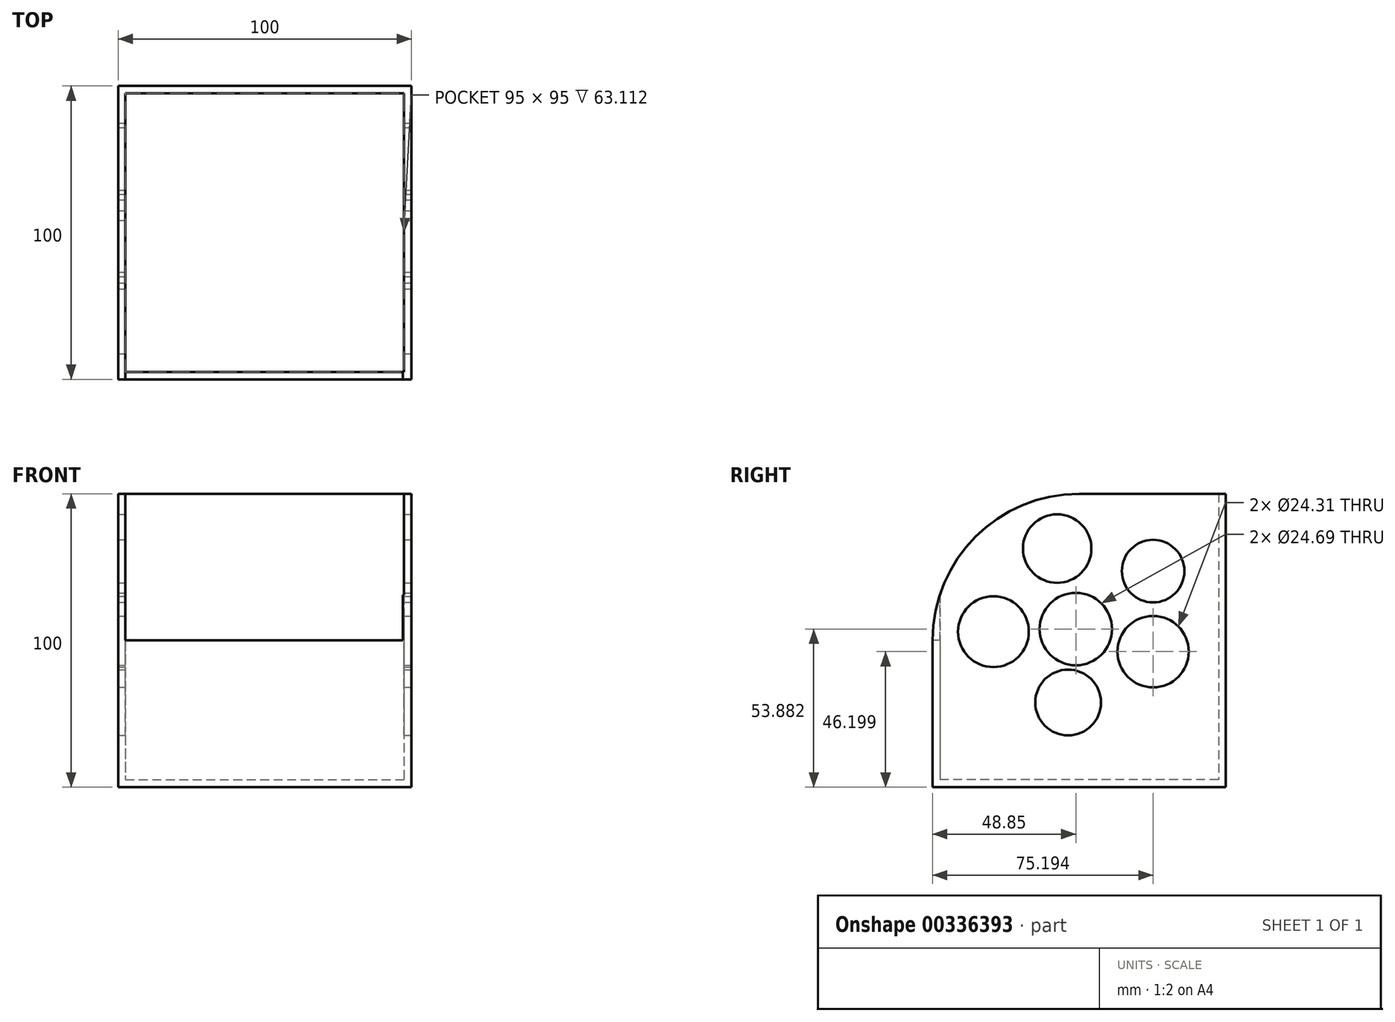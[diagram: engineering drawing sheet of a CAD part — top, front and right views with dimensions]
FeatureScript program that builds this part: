
annotation { "Feature Type Name" : "Feature", "Feature Type Description" : "" }
export const myFeature = defineFeature(function(context is Context, id is Id, definition is map)
    precondition{}
    {
        {
            var Q0;
            Q0=qCreatedBy(makeId("Top.planeOp"),FACE);
            var sketch = newSketch(context, id + "F0", { "sketchPlane" : qUnion([Q0])});
            skLineSegment(sketch, "E0.bottom", {"start": v(-69.43, 51.15) * mm, "end": v(30.57, 51.15) * mm});
            skLineSegment(sketch, "E0.top", {"start": v(-69.43, -48.85) * mm, "end": v(30.57, -48.85) * mm});
            skLineSegment(sketch, "E0.left", {"start": v(-69.43, 51.15) * mm, "end": v(-69.43, -48.85) * mm});
            skLineSegment(sketch, "E0.right", {"start": v(30.57, 51.15) * mm, "end": v(30.57, -48.85) * mm});
            skSolve(sketch);
        }
        {
            var Q0;
            Q0=makeQuery(id+"F0.imprint","IMPRINT",FACE,{"disambiguationData":[TD([[makeQuery(id+"F0.imprint","IMPRINT",EDGE,{"derivedFrom":sQuery(id+"F0.wireOp",EDGE,"E0.bottom")}),-1.0]])]});
            extrude(context, id + "F1", {"entities" : qUnion([Q0]), "depth" : 100 * mm});
        }
        {
            var Q0;
            Q0=makeQuery(id+"F1.opExtrude","CAP_FACE",FACE,{"disambiguationData":[OSD([sQuery(id+"F0.wireOp",EDGE,"E0.bottom"),sQuery(id+"F0.wireOp",EDGE,"E0.top"),sQuery(id+"F0.wireOp",EDGE,"E0.left"),sQuery(id+"F0.wireOp",EDGE,"E0.right")])],"isStart":false});
            shell(context, id + "F2", {"entities" : qUnion([Q0]), "thickness" : 2.5 * mm});
        }
        {
            var Q0;
            Q0=makeQuery(id+"F1.opExtrude","CAP_FACE",FACE,{"disambiguationData":[OSD([sQuery(id+"F0.wireOp",EDGE,"E0.bottom"),sQuery(id+"F0.wireOp",EDGE,"E0.top"),sQuery(id+"F0.wireOp",EDGE,"E0.left"),sQuery(id+"F0.wireOp",EDGE,"E0.right")])],"isStart":false});
            var sketch = newSketch(context, id + "F3", { "sketchPlane" : qUnion([Q0])});
            skLineSegment(sketch, "E1.bottom", {"start": v(-66.93, -30.87) * mm, "end": v(27.64, -30.87) * mm});
            skLineSegment(sketch, "E1.top", {"start": v(-66.93, -63.95) * mm, "end": v(27.64, -63.95) * mm});
            skLineSegment(sketch, "E1.left", {"start": v(-66.93, -30.87) * mm, "end": v(-66.93, -63.95) * mm});
            skLineSegment(sketch, "E1.right", {"start": v(27.64, -30.87) * mm, "end": v(27.64, -63.95) * mm});
            skSolve(sketch);
        }
        {
            var Q0;
            {var subQ0=sQuery(id+"F3.wireOp",EDGE,"E1.left");var subQ1=sQuery(id+"F0.wireOp",EDGE,"E0.top");var subQ2=makeQuery(id+"F1.opExtrude","CAP_EDGE",EDGE,{"disambiguationData":[OSD([subQ1])],"isStart":false});var subQ5=makeQuery(id+"F3.imprint","INTERSECT",VERTEX,{"derivedFrom":[subQ2,subQ0]});Q0=makeQuery(id+"F3.imprint","IMPRINT",FACE,{"disambiguationData":[TD([[makeQuery(id+"F3.imprint","IMPRINT",EDGE,{"disambiguationData":[TD([[subQ5,-1.0]])],"derivedFrom":subQ2}),1.0]])]});}
            extrude(context, id + "F4", {"entities" : qUnion([Q0]), "operationType" : NewBodyOperationType.REMOVE, "oppositeDirection" : true, "depth" : 50 * mm});
        }
        {
            var Q0;
            {var subQ0=sQuery(id+"F0.wireOp",EDGE,"E0.left");var subQ1=sQuery(id+"F0.wireOp",EDGE,"E0.top");Q0=makeQuery(id+"F4.boolean.opBoolean","SPLIT",EDGE,{"disambiguationData":[TD([makeQuery(id+"F1.opExtrude","SWEPT_FACE",FACE,{"disambiguationData":[OSD([subQ0])]})])],"derivedFrom":makeQuery(id+"F1.opExtrude","CAP_EDGE",EDGE,{"disambiguationData":[OSD([subQ1])],"isStart":false})});}
            var Q1;
            {var subQ0=sQuery(id+"F0.wireOp",EDGE,"E0.right");var subQ1=sQuery(id+"F0.wireOp",EDGE,"E0.top");Q1=makeQuery(id+"F4.boolean.opBoolean","SPLIT",EDGE,{"disambiguationData":[TD([makeQuery(id+"F1.opExtrude","SWEPT_FACE",FACE,{"disambiguationData":[OSD([subQ0])]})])],"derivedFrom":makeQuery(id+"F1.opExtrude","CAP_EDGE",EDGE,{"disambiguationData":[OSD([subQ1])],"isStart":false})});}
            fillet(context, id + "F5", {"entities" : qUnion([Q0, Q1]), "radius" : 50 * mm, "tangentPropagation" : true, "allowEdgeOverflow" : false});
        }
        {
            var Q0;
            Q0=makeQuery(id+"F1.opExtrude","SWEPT_FACE",FACE,{"disambiguationData":[OSD([sQuery(id+"F0.wireOp",EDGE,"E0.right")])]});
            var sketch = newSketch(context, id + "F6", { "sketchPlane" : qUnion([Q0])});
            skCircle(sketch, "E2", {"center": v(0, 53.88) * mm, "radius": 12.34 * mm});
            skCircle(sketch, "E3", {"center": v(26.34, 73.64) * mm, "radius": 10.66 * mm});
            skCircle(sketch, "E4", {"center": v(26.34, 46.2) * mm, "radius": 12.15 * mm});
            skCircle(sketch, "E5", {"center": v(-2.63, 28.86) * mm, "radius": 11.21 * mm});
            skCircle(sketch, "E6", {"center": v(-28.1, 53) * mm, "radius": 12.07 * mm});
            skCircle(sketch, "E7", {"center": v(-6.37, 81.32) * mm, "radius": 11.67 * mm});
            skSolve(sketch);
        }
        {
            var Q0;
            Q0=makeQuery(id+"F6.imprint","IMPRINT",FACE,{"disambiguationData":[TD([[makeQuery(id+"F6.imprint","IMPRINT",EDGE,{"derivedFrom":sQuery(id+"F6.wireOp",EDGE,"E6")}),1.0]])]});
            var Q1;
            Q1=makeQuery(id+"F6.imprint","IMPRINT",FACE,{"disambiguationData":[TD([[makeQuery(id+"F6.imprint","IMPRINT",EDGE,{"derivedFrom":sQuery(id+"F6.wireOp",EDGE,"E5")}),1.0]])]});
            var Q2;
            Q2=makeQuery(id+"F6.imprint","IMPRINT",FACE,{"disambiguationData":[TD([[makeQuery(id+"F6.imprint","IMPRINT",EDGE,{"derivedFrom":sQuery(id+"F6.wireOp",EDGE,"E2")}),1.0]])]});
            var Q3;
            Q3=makeQuery(id+"F6.imprint","IMPRINT",FACE,{"disambiguationData":[TD([[makeQuery(id+"F6.imprint","IMPRINT",EDGE,{"derivedFrom":sQuery(id+"F6.wireOp",EDGE,"E7")}),1.0]])]});
            var Q4;
            Q4=makeQuery(id+"F6.imprint","IMPRINT",FACE,{"disambiguationData":[TD([[makeQuery(id+"F6.imprint","IMPRINT",EDGE,{"derivedFrom":sQuery(id+"F6.wireOp",EDGE,"E3")}),1.0]])]});
            var Q5;
            Q5=makeQuery(id+"F6.imprint","IMPRINT",FACE,{"disambiguationData":[TD([[makeQuery(id+"F6.imprint","IMPRINT",EDGE,{"derivedFrom":sQuery(id+"F6.wireOp",EDGE,"E4")}),1.0]])]});
            extrude(context, id + "F7", {"entities" : qUnion([Q0, Q1, Q2, Q3, Q4, Q5]), "operationType" : NewBodyOperationType.REMOVE, "endBound" : BoundingType.THROUGH_ALL, "oppositeDirection" : true, "depth" : 25 * mm});
        }
    });
